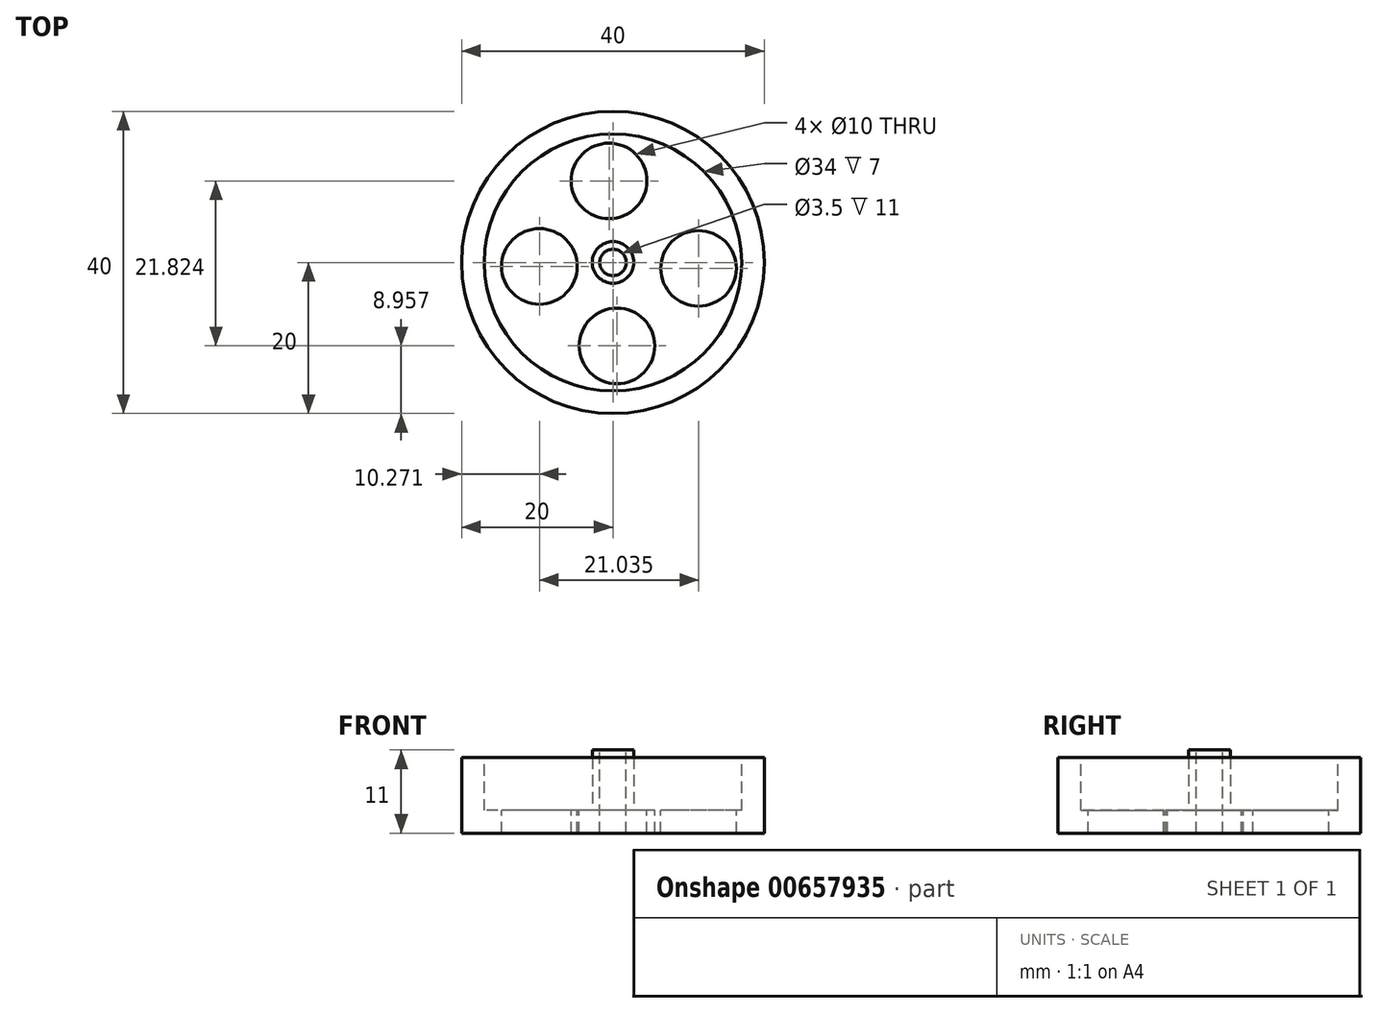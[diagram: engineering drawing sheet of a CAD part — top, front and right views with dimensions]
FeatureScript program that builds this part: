
annotation { "Feature Type Name" : "Feature", "Feature Type Description" : "" }
export const myFeature = defineFeature(function(context is Context, id is Id, definition is map)
    precondition{}
    {
        {
            var Q0;
            Q0=qCreatedBy(makeId("Top.planeOp"),FACE);
            var sketch = newSketch(context, id + "F0", { "sketchPlane" : qUnion([Q0])});
            skCircle(sketch, "E0", {"center": v(0, 0) * mm, "radius": 20 * mm});
            skSolve(sketch);
        }
        {
            var Q0;
            Q0 = qSketchRegion(id + "F0", true);
            extrude(context, id + "F1", {"entities" : qUnion([Q0]), "oppositeDirection" : true, "depth" : 10 * mm, "offsetDistance" : 25 * mm});
        }
        {
            var Q0;
            Q0=makeQuery(id+"F1.opExtrude","CAP_FACE",FACE,{"disambiguationData":[OSD([sQuery(id+"F0.wireOp",EDGE,"E0")])],"isStart":true});
            shell(context, id + "F2", {"entities" : qUnion([Q0]), "thickness" : 3 * mm});
        }
        {
            var Q0;
            Q0=qCreatedBy(makeId("Top.planeOp"),FACE);
            var sketch = newSketch(context, id + "F3", { "sketchPlane" : qUnion([Q0])});
            skCircle(sketch, "E1", {"center": v(0, 0) * mm, "radius": 3.25 * mm});
            skSolve(sketch);
        }
        {
            var Q0;
            Q0=sQuery(id+"F3.wireOp",EDGE,"E1");
            extrude(context, id + "F4", {"bodyType" : ToolBodyType.SURFACE, "surfaceEntities" : qUnion([Q0]), "oppositeDirection" : true, "depth" : 7 * mm, "offsetDistance" : 25 * mm});
        }
        {
            var Q0;
            Q0=makeQuery(id+"F4.opExtrude","SWEPT_BODY",BODY,{"disambiguationData":[OSD([sQuery(id+"F3.wireOp",EDGE,"E1")])]});
            deleteBodies(context, id + "F5", {"entities" : qUnion([Q0])});
        }
        {
            var Q0;
            {var subQ0=sQuery(id+"F0.wireOp",EDGE,"E0");Q0=makeQuery(id+"F2.opShell","OFFSET_FACE",FACE,{"disambiguationData":[OSD([subQ0]),TDD([makeQuery(id+"F1.opExtrude","CAP_FACE",FACE,{"disambiguationData":[OSD([subQ0])],"isStart":false})])]});}
            var sketch = newSketch(context, id + "F6", { "sketchPlane" : qUnion([Q0])});
            skCircle(sketch, "E2", {"center": v(0, 0) * mm, "radius": 2.75 * mm});
            skSolve(sketch);
        }
        {
            var Q0;
            Q0=makeQuery(id+"F6.imprint","IMPRINT",FACE,{"disambiguationData":[TD([[makeQuery(id+"F6.imprint","IMPRINT",EDGE,{"derivedFrom":sQuery(id+"F6.wireOp",EDGE,"E2")}),1.0]])]});
            extrude(context, id + "F7", {"entities" : qUnion([Q0]), "operationType" : NewBodyOperationType.ADD, "depth" : 8 * mm, "offsetDistance" : 25 * mm});
        }
        {
            var Q0;
            Q0=makeQuery(id+"F7.opExtrude","CAP_FACE",FACE,{"disambiguationData":[OSD([sQuery(id+"F6.wireOp",EDGE,"E2")])],"isStart":false});
            var sketch = newSketch(context, id + "F8", { "sketchPlane" : qUnion([Q0])});
            skPoint(sketch, "E3", {"position": v(0, 0) * mm});
            skSolve(sketch);
        }
        {
            var Q0;
            Q0=sQuery(id+"F8.wireOp",VERTEX,"E3");
            var Q1;
            Q1=makeQuery(id+"F1.opExtrude","SWEPT_BODY",BODY,{"disambiguationData":[OSD([sQuery(id+"F0.wireOp",EDGE,"E0")])]});
            hole(context, id + "F9", {"style" : HoleStyle.SIMPLE, "endStyle" : HoleEndStyle.THROUGH, "holeDiameter" : 3.5 * mm, "majorDiameter" : 5 * mm, "isTappedThrough" : true, "tappedDepth" : 12 * mm, "tapClearance" : 3, "locations" : qUnion([Q0]), "scope" : qUnion([Q1])});
        }
        {
            var Q0;
            Q0=makeQuery(id+"F0.imprint","IMPRINT",FACE,{"disambiguationData":[TD([[makeQuery(id+"F0.imprint","IMPRINT",EDGE,{"derivedFrom":sQuery(id+"F0.wireOp",EDGE,"E0")}),1.0]])]});
            var sketch = newSketch(context, id + "F10", { "sketchPlane" : qUnion([Q0])});
            skPoint(sketch, "E4", {"position": v(-0.53, 10.78) * mm});
            skPoint(sketch, "E5", {"position": v(-13.15, -1.31) * mm});
            skPoint(sketch, "E6", {"position": v(0.79, -12.1) * mm});
            skPoint(sketch, "E7", {"position": v(11.04, -1.05) * mm});
            skSolve(sketch);
        }
        {
            var Q0;
            Q0=sQuery(id+"F10.wireOp",VERTEX,"E4");
            var Q1;
            Q1=makeQuery(id+"F1.opExtrude","SWEPT_BODY",BODY,{"disambiguationData":[OSD([sQuery(id+"F0.wireOp",EDGE,"E0")])]});
            hole(context, id + "F11", {"style" : HoleStyle.SIMPLE, "endStyle" : HoleEndStyle.THROUGH, "holeDiameter" : 10 * mm, "majorDiameter" : 5 * mm, "isTappedThrough" : true, "tappedDepth" : 12 * mm, "tapClearance" : 3, "locations" : qUnion([Q0]), "scope" : qUnion([Q1])});
        }
        {
            var Q0;
            Q0=makeQuery(id+"F0.imprint","IMPRINT",FACE,{"disambiguationData":[TD([[makeQuery(id+"F0.imprint","IMPRINT",EDGE,{"derivedFrom":sQuery(id+"F0.wireOp",EDGE,"E0")}),1.0]])]});
            var sketch = newSketch(context, id + "F12", { "sketchPlane" : qUnion([Q0])});
            skPoint(sketch, "E8", {"position": v(-9.73, -0.53) * mm});
            skSolve(sketch);
        }
        {
            var Q0;
            Q0=sQuery(id+"F12.wireOp",VERTEX,"E8");
            var Q1;
            Q1=makeQuery(id+"F1.opExtrude","SWEPT_BODY",BODY,{"disambiguationData":[OSD([sQuery(id+"F0.wireOp",EDGE,"E0")])]});
            hole(context, id + "F13", {"style" : HoleStyle.SIMPLE, "endStyle" : HoleEndStyle.THROUGH, "holeDiameter" : 10 * mm, "majorDiameter" : 5 * mm, "isTappedThrough" : true, "tappedDepth" : 12 * mm, "tapClearance" : 3, "locations" : qUnion([Q0]), "scope" : qUnion([Q1])});
        }
        {
            var Q0;
            Q0=makeQuery(id+"F0.imprint","IMPRINT",FACE,{"disambiguationData":[TD([[makeQuery(id+"F0.imprint","IMPRINT",EDGE,{"derivedFrom":sQuery(id+"F0.wireOp",EDGE,"E0")}),1.0]])]});
            var sketch = newSketch(context, id + "F14", { "sketchPlane" : qUnion([Q0])});
            skPoint(sketch, "E9", {"position": v(0.53, -11.04) * mm});
            skSolve(sketch);
        }
        {
            var Q0;
            Q0=sQuery(id+"F14.wireOp",VERTEX,"E9");
            var Q1;
            Q1=makeQuery(id+"F1.opExtrude","SWEPT_BODY",BODY,{"disambiguationData":[OSD([sQuery(id+"F0.wireOp",EDGE,"E0")])]});
            hole(context, id + "F15", {"style" : HoleStyle.SIMPLE, "endStyle" : HoleEndStyle.THROUGH, "holeDiameter" : 10 * mm, "majorDiameter" : 5 * mm, "isTappedThrough" : true, "tappedDepth" : 12 * mm, "tapClearance" : 3, "locations" : qUnion([Q0]), "scope" : qUnion([Q1])});
        }
        {
            var Q0;
            Q0=makeQuery(id+"F0.imprint","IMPRINT",FACE,{"disambiguationData":[TD([[makeQuery(id+"F0.imprint","IMPRINT",EDGE,{"derivedFrom":sQuery(id+"F0.wireOp",EDGE,"E0")}),1.0]])]});
            var sketch = newSketch(context, id + "F16", { "sketchPlane" : qUnion([Q0])});
            skPoint(sketch, "E10", {"position": v(11.3, -0.79) * mm});
            skSolve(sketch);
        }
        {
            var Q0;
            Q0=sQuery(id+"F16.wireOp",VERTEX,"E10");
            var Q1;
            Q1=makeQuery(id+"F1.opExtrude","SWEPT_BODY",BODY,{"disambiguationData":[OSD([sQuery(id+"F0.wireOp",EDGE,"E0")])]});
            hole(context, id + "F17", {"style" : HoleStyle.SIMPLE, "endStyle" : HoleEndStyle.THROUGH, "holeDiameter" : 10 * mm, "majorDiameter" : 5 * mm, "isTappedThrough" : true, "tappedDepth" : 12 * mm, "tapClearance" : 3, "locations" : qUnion([Q0]), "scope" : qUnion([Q1])});
        }
    });
